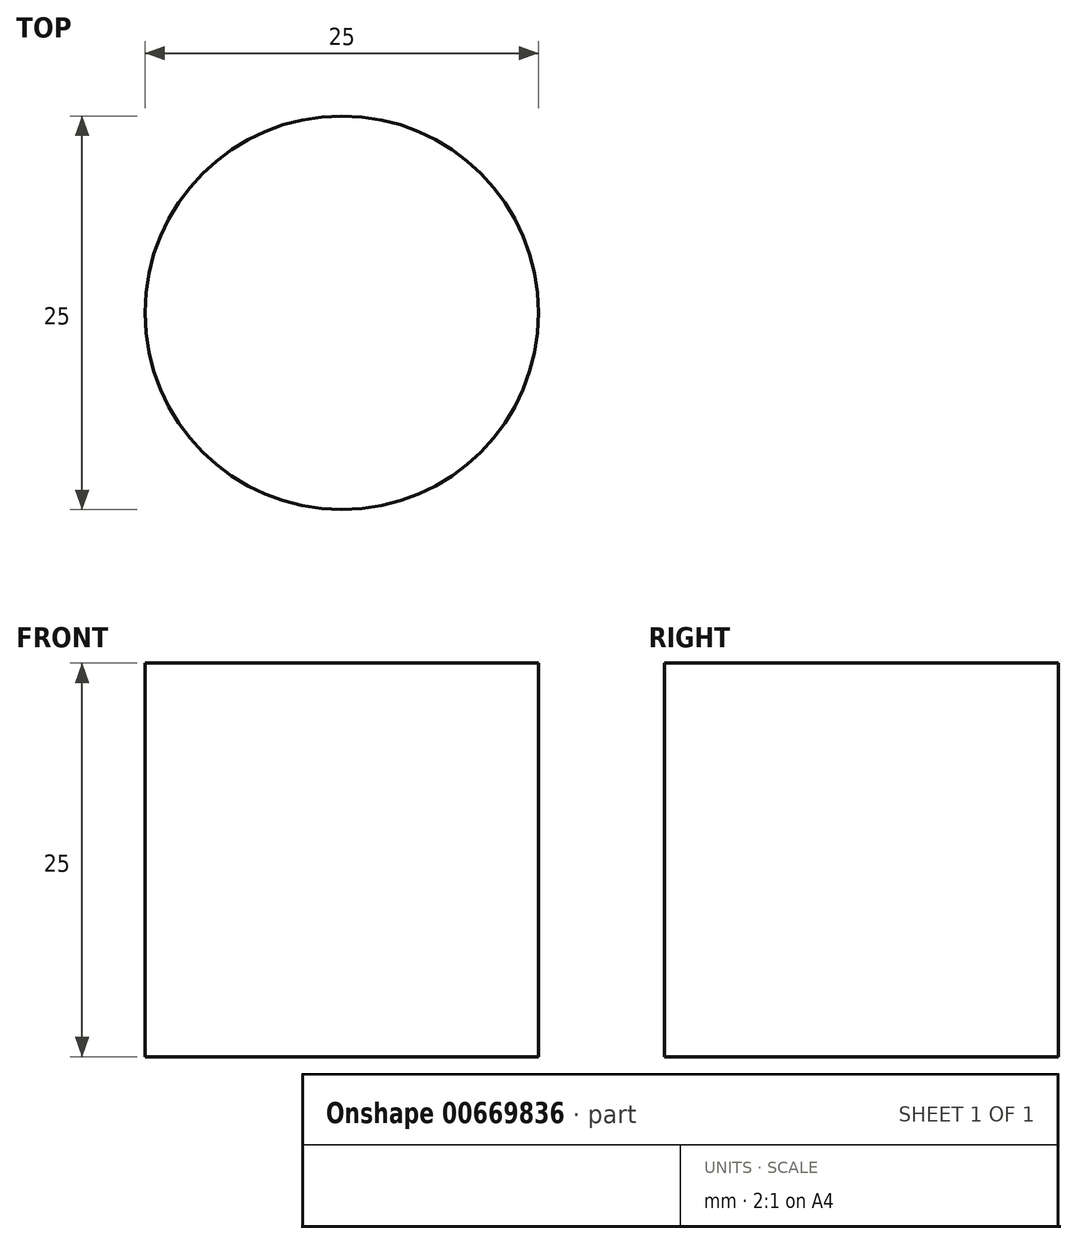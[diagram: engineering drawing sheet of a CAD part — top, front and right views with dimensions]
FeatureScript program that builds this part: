
annotation { "Feature Type Name" : "Feature", "Feature Type Description" : "" }
export const myFeature = defineFeature(function(context is Context, id is Id, definition is map)
    precondition{}
    {
        {
            var Q0;
            Q0=qCreatedBy(makeId("Top.planeOp"),FACE);
            var sketch = newSketch(context, id + "F0", { "sketchPlane" : qUnion([Q0])});
            skCircle(sketch, "E0", {"center": v(0, 0) * mm, "radius": 12.5 * mm});
            skSolve(sketch);
        }
        {
            var Q0;
            Q0=qCreatedBy(makeId("Top.planeOp"),FACE);
            var sketch = newSketch(context, id + "F1", { "sketchPlane" : qUnion([Q0])});
            skCircle(sketch, "E1", {"center": v(0, 0) * mm, "radius": 11.75 * mm});
            skSolve(sketch);
        }
        {
            var Q0;
            Q0=makeQuery(id+"F0.imprint","IMPRINT",FACE,{"disambiguationData":[TD([[makeQuery(id+"F0.imprint","IMPRINT",EDGE,{"derivedFrom":sQuery(id+"F0.wireOp",EDGE,"E0")}),1.0]])]});
            var Q1;
            Q1=sQuery(id+"F1.wireOp",EDGE,"E1");
            extrude(context, id + "F2", {"entities" : qUnion([Q0]), "surfaceEntities" : qUnion([Q1]), "depth" : 25 * mm, "offsetDistance" : 25 * mm});
        }
    });
